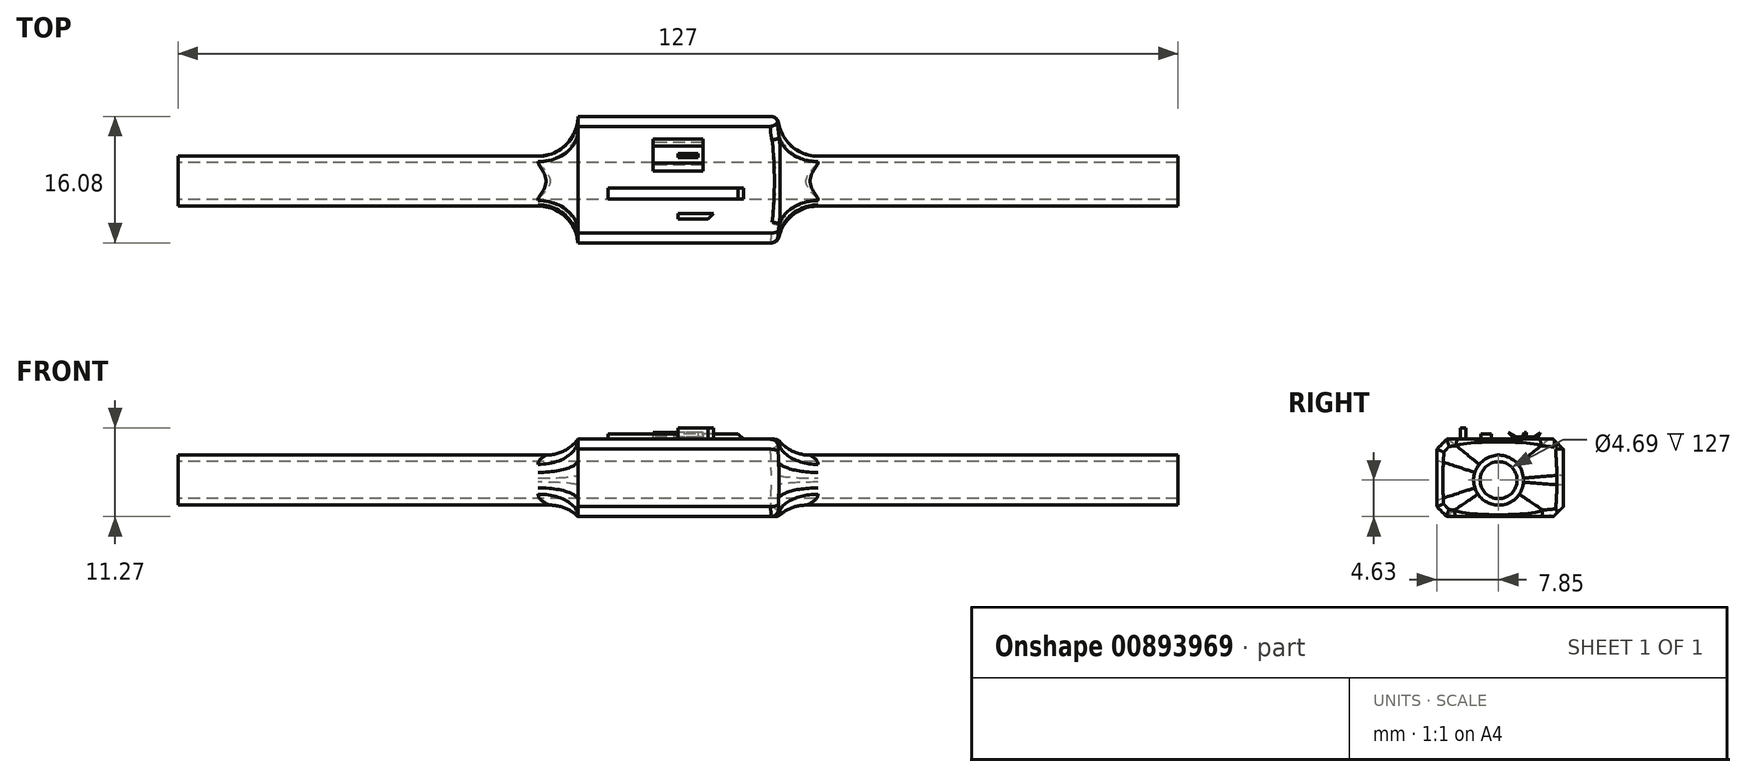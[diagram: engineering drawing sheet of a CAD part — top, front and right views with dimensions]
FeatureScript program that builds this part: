
annotation { "Feature Type Name" : "Feature", "Feature Type Description" : "" }
export const myFeature = defineFeature(function(context is Context, id is Id, definition is map)
    precondition{}
    {
        {
            var Q0;
            Q0=qCreatedBy(makeId("Right.planeOp"),FACE);
            var sketch = newSketch(context, id + "F0", { "sketchPlane" : qUnion([Q0])});
            skCircle(sketch, "E0", {"center": v(0, 0) * mm, "radius": 3.18 * mm});
            skCircle(sketch, "E1", {"center": v(0, 0) * mm, "radius": 2.35 * mm});
            skSolve(sketch);
        }
        {
            var Q0;
            Q0=makeQuery(id+"F0.imprint","IMPRINT",FACE,{"disambiguationData":[TD([[makeQuery(id+"F0.imprint","IMPRINT",EDGE,{"derivedFrom":sQuery(id+"F0.wireOp",EDGE,"E0")}),1.0]])]});
            extrude(context, id + "F1", {"entities" : qUnion([Q0]), "endBound" : BoundingType.SYMMETRIC, "depth" : 127 * mm, "offsetDistance" : 25.4 * mm});
        }
        {
            var Q0;
            Q0=qCreatedBy(makeId("Right.planeOp"),FACE);
            var sketch = newSketch(context, id + "F2", { "sketchPlane" : qUnion([Q0])});
            skLineSegment(sketch, "E2.bottom", {"start": v(-7.85, -4.63) * mm, "end": v(8.23, -4.63) * mm});
            skLineSegment(sketch, "E2.top", {"start": v(-7.85, 5.2) * mm, "end": v(8.23, 5.2) * mm});
            skLineSegment(sketch, "E2.left", {"start": v(-7.85, -4.63) * mm, "end": v(-7.85, 5.2) * mm});
            skLineSegment(sketch, "E2.right", {"start": v(8.23, -4.63) * mm, "end": v(8.23, 5.2) * mm});
            skLineSegment(sketch, "E3", {"start": v(-4.82, 5.2) * mm, "end": v(-4.82, 6.64) * mm});
            skLineSegment(sketch, "E4", {"start": v(-4.82, 6.64) * mm, "end": v(-4.13, 6.64) * mm});
            skLineSegment(sketch, "E5", {"start": v(-4.13, 6.64) * mm, "end": v(-4.13, 5.2) * mm});
            skLineSegment(sketch, "E6", {"start": v(-2.28, 5.2) * mm, "end": v(-2.28, 5.87) * mm});
            skLineSegment(sketch, "E7", {"start": v(-2.28, 5.87) * mm, "end": v(-0.89, 5.87) * mm});
            skLineSegment(sketch, "E8", {"start": v(-0.89, 5.87) * mm, "end": v(-0.89, 5.2) * mm});
            skLineSegment(sketch, "E9", {"start": v(1.27, 6.03) * mm, "end": v(2.06, 5.2) * mm});
            skLineSegment(sketch, "E10", {"start": v(2.06, 5.2) * mm, "end": v(4.9, 5.2) * mm});
            skLineSegment(sketch, "E11", {"start": v(4.9, 5.2) * mm, "end": v(5.31, 6.08) * mm});
            skLineSegment(sketch, "E12", {"start": v(5.31, 6.08) * mm, "end": v(4.47, 5.5) * mm});
            skLineSegment(sketch, "E13", {"start": v(4.47, 5.5) * mm, "end": v(2.3, 5.5) * mm});
            skLineSegment(sketch, "E14", {"start": v(2.3, 5.5) * mm, "end": v(1.27, 6.03) * mm});
            skLineSegment(sketch, "E15", {"start": v(3, 5.5) * mm, "end": v(3.25, 6.03) * mm});
            skLineSegment(sketch, "E16", {"start": v(3.25, 6.03) * mm, "end": v(3.53, 6.03) * mm});
            skLineSegment(sketch, "E17", {"start": v(3.53, 6.03) * mm, "end": v(3.53, 5.5) * mm});
            skCircle(sketch, "E18", {"center": v(0, 0) * mm, "radius": 3.16 * mm});
            skSolve(sketch);
        }
        {
            var Q0;
            Q0=makeQuery(id+"F2.imprint","IMPRINT",FACE,{"disambiguationData":[TD([[makeQuery(id+"F2.imprint","IMPRINT",EDGE,{"derivedFrom":sQuery(id+"F2.wireOp",EDGE,"E2.bottom")}),1.0]])]});
            extrude(context, id + "F3", {"entities" : qUnion([Q0]), "operationType" : NewBodyOperationType.ADD, "endBound" : BoundingType.SYMMETRIC, "depth" : 25.4 * mm, "offsetDistance" : 25.4 * mm});
        }
        {
            var Q0;
            {var subQ0=sQuery(id+"F2.wireOp",EDGE,"E3");Q0=makeQuery(id+"F2.imprint","IMPRINT",FACE,{"disambiguationData":[TD([[makeQuery(id+"F2.imprint","IMPRINT",EDGE,{"derivedFrom":subQ0}),-1.0]])]});}
            extrude(context, id + "F4", {"entities" : qUnion([Q0]), "operationType" : NewBodyOperationType.ADD, "depth" : 5.08 * mm, "offsetDistance" : 25.4 * mm});
        }
        {
            var Q0;
            {var subQ0=sQuery(id+"F2.wireOp",EDGE,"E6");Q0=makeQuery(id+"F2.imprint","IMPRINT",FACE,{"disambiguationData":[TD([[makeQuery(id+"F2.imprint","IMPRINT",EDGE,{"derivedFrom":subQ0}),-1.0]])]});}
            extrude(context, id + "F5", {"entities" : qUnion([Q0]), "operationType" : NewBodyOperationType.ADD, "endBound" : BoundingType.SYMMETRIC, "depth" : 17.78 * mm, "offsetDistance" : 25.4 * mm});
        }
        {
            var Q0;
            Q0=makeQuery(id+"F2.imprint","IMPRINT",FACE,{"disambiguationData":[TD([[makeQuery(id+"F2.imprint","IMPRINT",EDGE,{"derivedFrom":sQuery(id+"F2.wireOp",EDGE,"E9")}),1.0]])]});
            extrude(context, id + "F6", {"entities" : qUnion([Q0]), "operationType" : NewBodyOperationType.ADD, "endBound" : BoundingType.SYMMETRIC, "depth" : 6.35 * mm, "offsetDistance" : 25.4 * mm});
        }
        {
            var Q0;
            {var subQ0=sQuery(id+"F2.wireOp",EDGE,"E15");Q0=makeQuery(id+"F2.imprint","IMPRINT",FACE,{"disambiguationData":[TD([[makeQuery(id+"F2.imprint","IMPRINT",EDGE,{"derivedFrom":subQ0}),-1.0]])]});}
            extrude(context, id + "F7", {"entities" : qUnion([Q0]), "operationType" : NewBodyOperationType.ADD, "depth" : 2.54 * mm, "offsetDistance" : 25.4 * mm});
        }
        {
            var Q0;
            Q0=makeQuery(id+"F3.boolean.opBoolean","INTERSECT",EDGE,{"derivedFrom":[makeQuery(id+"F1.opExtrude","SWEPT_FACE",FACE,{"disambiguationData":[OSD([sQuery(id+"F0.wireOp",EDGE,"E0")])]}),makeQuery(id+"F3.opExtrude","CAP_FACE",FACE,{"disambiguationData":[OSD([sQuery(id+"F2.wireOp",EDGE,"E2.bottom"),sQuery(id+"F2.wireOp",EDGE,"E2.top"),sQuery(id+"F2.wireOp",EDGE,"E2.left"),sQuery(id+"F2.wireOp",EDGE,"E2.right"),sQuery(id+"F2.wireOp",EDGE,"E10")])],"isStart":false})]});
            var Q1;
            Q1=makeQuery(id+"F3.boolean.opBoolean","INTERSECT",EDGE,{"derivedFrom":[makeQuery(id+"F1.opExtrude","SWEPT_FACE",FACE,{"disambiguationData":[OSD([sQuery(id+"F0.wireOp",EDGE,"E0")])]}),makeQuery(id+"F3.opExtrude","CAP_FACE",FACE,{"disambiguationData":[OSD([sQuery(id+"F2.wireOp",EDGE,"E2.bottom"),sQuery(id+"F2.wireOp",EDGE,"E2.top"),sQuery(id+"F2.wireOp",EDGE,"E2.left"),sQuery(id+"F2.wireOp",EDGE,"E2.right"),sQuery(id+"F2.wireOp",EDGE,"E10")])],"isStart":true})]});
            fillet(context, id + "F8", {"entities" : qUnion([Q0, Q1]), "radius" : 5.08 * mm, "tangentPropagation" : true, "allowEdgeOverflow" : false});
        }
        {
            var Q0;
            Q0=makeQuery(id+"F3.opExtrude","SWEPT_EDGE",EDGE,{"disambiguationData":[OSD([sQuery(id+"F2.wireOp",EDGE,"E2.top"),sQuery(id+"F2.wireOp",EDGE,"E2.right")])]});
            var Q1;
            Q1=makeQuery(id+"F3.opExtrude","SWEPT_EDGE",EDGE,{"disambiguationData":[OSD([sQuery(id+"F2.wireOp",EDGE,"E2.bottom"),sQuery(id+"F2.wireOp",EDGE,"E2.right")])]});
            var Q2;
            Q2=makeQuery(id+"F3.opExtrude","SWEPT_EDGE",EDGE,{"disambiguationData":[OSD([sQuery(id+"F2.wireOp",EDGE,"E2.top"),sQuery(id+"F2.wireOp",EDGE,"E2.left")])]});
            var Q3;
            Q3=makeQuery(id+"F3.opExtrude","SWEPT_EDGE",EDGE,{"disambiguationData":[OSD([sQuery(id+"F2.wireOp",EDGE,"E2.bottom"),sQuery(id+"F2.wireOp",EDGE,"E2.left")])]});
            var Q4;
            Q4=makeQuery(id+"F4.opExtrude","CAP_EDGE",EDGE,{"disambiguationData":[OSD([sQuery(id+"F2.wireOp",EDGE,"E3")])],"isStart":false});
            var Q5;
            Q5=makeQuery(id+"F5.opExtrude","CAP_EDGE",EDGE,{"disambiguationData":[OSD([sQuery(id+"F2.wireOp",EDGE,"E7")])],"isStart":false});
            chamfer(context, id + "F9", {"entities" : qUnion([Q0, Q1, Q2, Q3, Q4, Q5]), "width" : 1.27 * mm, "tangentPropagation" : true});
        }
        {
            var Q0;
            {var subQ0=sQuery(id+"F2.wireOp",EDGE,"E10");var subQ1=sQuery(id+"F2.wireOp",EDGE,"E2.top");Q0=makeQuery(id+"F8.opFillet","BLEND_EDGE",EDGE,{"blendedFrom":[makeQuery(id+"F3.boolean.opBoolean","INTERSECT",EDGE,{"derivedFrom":[makeQuery(id+"F1.opExtrude","SWEPT_FACE",FACE,{"disambiguationData":[OSD([sQuery(id+"F0.wireOp",EDGE,"E0")])]}),makeQuery(id+"F3.opExtrude","CAP_FACE",FACE,{"disambiguationData":[OSD([sQuery(id+"F2.wireOp",EDGE,"E2.bottom"),subQ1,sQuery(id+"F2.wireOp",EDGE,"E2.left"),sQuery(id+"F2.wireOp",EDGE,"E2.right"),subQ0,sQuery(id+"F2.wireOp",EDGE,"E18")])],"isStart":false})]}),makeQuery(id+"F3.opExtrude","SWEPT_FACE",FACE,{"disambiguationData":[OSD([subQ1,subQ0])]})],"blendedInto":[makeQuery(id+"F3.opExtrude","SWEPT_FACE",FACE,{"disambiguationData":[OSD([subQ1,subQ0])]})]});}
            var Q1;
            {var subQ0=sQuery(id+"F2.wireOp",EDGE,"E2.left");var subQ1=sQuery(id+"F2.wireOp",EDGE,"E2.top");Q1=makeQuery(id+"F9.opChamfer","BLEND_EDGE",EDGE,{"blendedFrom":[makeQuery(id+"F3.opExtrude","SWEPT_EDGE",EDGE,{"disambiguationData":[OSD([subQ1,subQ0])]}),makeQuery(id+"F8.opFillet","SPLIT",FACE,{"disambiguationData":[OD(2.0)],"derivedFrom":makeQuery(id+"F3.opExtrude","CAP_FACE",FACE,{"disambiguationData":[OSD([sQuery(id+"F2.wireOp",EDGE,"E2.bottom"),subQ1,subQ0,sQuery(id+"F2.wireOp",EDGE,"E2.right"),sQuery(id+"F2.wireOp",EDGE,"E10"),sQuery(id+"F2.wireOp",EDGE,"E18")])],"isStart":false})})],"blendedInto":[makeQuery(id+"F8.opFillet","SPLIT",FACE,{"disambiguationData":[OD(2.0)],"derivedFrom":makeQuery(id+"F3.opExtrude","CAP_FACE",FACE,{"disambiguationData":[OSD([sQuery(id+"F2.wireOp",EDGE,"E2.bottom"),subQ1,subQ0,sQuery(id+"F2.wireOp",EDGE,"E2.right"),sQuery(id+"F2.wireOp",EDGE,"E10"),sQuery(id+"F2.wireOp",EDGE,"E18")])],"isStart":false})})]});}
            var Q2;
            {var subQ0=sQuery(id+"F2.wireOp",EDGE,"E2.left");Q2=makeQuery(id+"F8.opFillet","BLEND_EDGE",EDGE,{"blendedFrom":[makeQuery(id+"F3.boolean.opBoolean","INTERSECT",EDGE,{"derivedFrom":[makeQuery(id+"F1.opExtrude","SWEPT_FACE",FACE,{"disambiguationData":[OSD([sQuery(id+"F0.wireOp",EDGE,"E0")])]}),makeQuery(id+"F3.opExtrude","CAP_FACE",FACE,{"disambiguationData":[OSD([sQuery(id+"F2.wireOp",EDGE,"E2.bottom"),sQuery(id+"F2.wireOp",EDGE,"E2.top"),subQ0,sQuery(id+"F2.wireOp",EDGE,"E2.right"),sQuery(id+"F2.wireOp",EDGE,"E10"),sQuery(id+"F2.wireOp",EDGE,"E18")])],"isStart":false})]}),makeQuery(id+"F3.opExtrude","SWEPT_FACE",FACE,{"disambiguationData":[OSD([subQ0])]})],"blendedInto":[makeQuery(id+"F3.opExtrude","SWEPT_FACE",FACE,{"disambiguationData":[OSD([subQ0])]})]});}
            var Q3;
            Q3=makeQuery(id+"F3.opExtrude","CAP_EDGE",EDGE,{"disambiguationData":[OSD([sQuery(id+"F2.wireOp",EDGE,"E2.left")])],"isStart":false});
            var Q4;
            {var subQ0=sQuery(id+"F2.wireOp",EDGE,"E2.right");var subQ1=sQuery(id+"F2.wireOp",EDGE,"E2.top");Q4=makeQuery(id+"F9.opChamfer","BLEND_EDGE",EDGE,{"blendedFrom":[makeQuery(id+"F3.opExtrude","SWEPT_EDGE",EDGE,{"disambiguationData":[OSD([subQ1,subQ0])]}),makeQuery(id+"F8.opFillet","SPLIT",FACE,{"disambiguationData":[OD(1.0)],"derivedFrom":makeQuery(id+"F3.opExtrude","CAP_FACE",FACE,{"disambiguationData":[OSD([sQuery(id+"F2.wireOp",EDGE,"E2.bottom"),subQ1,sQuery(id+"F2.wireOp",EDGE,"E2.left"),subQ0,sQuery(id+"F2.wireOp",EDGE,"E10"),sQuery(id+"F2.wireOp",EDGE,"E18")])],"isStart":false})})],"blendedInto":[makeQuery(id+"F8.opFillet","SPLIT",FACE,{"disambiguationData":[OD(1.0)],"derivedFrom":makeQuery(id+"F3.opExtrude","CAP_FACE",FACE,{"disambiguationData":[OSD([sQuery(id+"F2.wireOp",EDGE,"E2.bottom"),subQ1,sQuery(id+"F2.wireOp",EDGE,"E2.left"),subQ0,sQuery(id+"F2.wireOp",EDGE,"E10"),sQuery(id+"F2.wireOp",EDGE,"E18")])],"isStart":false})})]});}
            var Q5;
            Q5=makeQuery(id+"F3.opExtrude","CAP_EDGE",EDGE,{"disambiguationData":[OSD([sQuery(id+"F2.wireOp",EDGE,"E2.top"),sQuery(id+"F2.wireOp",EDGE,"E10")])],"isStart":false});
            var Q6;
            {var subQ0=sQuery(id+"F2.wireOp",EDGE,"E2.right");Q6=makeQuery(id+"F8.opFillet","BLEND_EDGE",EDGE,{"blendedFrom":[makeQuery(id+"F3.boolean.opBoolean","INTERSECT",EDGE,{"derivedFrom":[makeQuery(id+"F1.opExtrude","SWEPT_FACE",FACE,{"disambiguationData":[OSD([sQuery(id+"F0.wireOp",EDGE,"E0")])]}),makeQuery(id+"F3.opExtrude","CAP_FACE",FACE,{"disambiguationData":[OSD([sQuery(id+"F2.wireOp",EDGE,"E2.bottom"),sQuery(id+"F2.wireOp",EDGE,"E2.top"),sQuery(id+"F2.wireOp",EDGE,"E2.left"),subQ0,sQuery(id+"F2.wireOp",EDGE,"E10"),sQuery(id+"F2.wireOp",EDGE,"E18")])],"isStart":false})]}),makeQuery(id+"F3.opExtrude","SWEPT_FACE",FACE,{"disambiguationData":[OSD([subQ0])]})],"blendedInto":[makeQuery(id+"F3.opExtrude","SWEPT_FACE",FACE,{"disambiguationData":[OSD([subQ0])]})]});}
            var Q7;
            Q7=makeQuery(id+"F3.opExtrude","CAP_EDGE",EDGE,{"disambiguationData":[OSD([sQuery(id+"F2.wireOp",EDGE,"E2.right")])],"isStart":false});
            var Q8;
            {var subQ0=sQuery(id+"F2.wireOp",EDGE,"E2.right");var subQ1=sQuery(id+"F2.wireOp",EDGE,"E2.bottom");Q8=makeQuery(id+"F9.opChamfer","BLEND_EDGE",EDGE,{"blendedFrom":[makeQuery(id+"F3.opExtrude","SWEPT_EDGE",EDGE,{"disambiguationData":[OSD([subQ1,subQ0])]}),makeQuery(id+"F8.opFillet","SPLIT",FACE,{"disambiguationData":[OD(0.0)],"derivedFrom":makeQuery(id+"F3.opExtrude","CAP_FACE",FACE,{"disambiguationData":[OSD([subQ1,sQuery(id+"F2.wireOp",EDGE,"E2.top"),sQuery(id+"F2.wireOp",EDGE,"E2.left"),subQ0,sQuery(id+"F2.wireOp",EDGE,"E10"),sQuery(id+"F2.wireOp",EDGE,"E18")])],"isStart":false})})],"blendedInto":[makeQuery(id+"F8.opFillet","SPLIT",FACE,{"disambiguationData":[OD(0.0)],"derivedFrom":makeQuery(id+"F3.opExtrude","CAP_FACE",FACE,{"disambiguationData":[OSD([subQ1,sQuery(id+"F2.wireOp",EDGE,"E2.top"),sQuery(id+"F2.wireOp",EDGE,"E2.left"),subQ0,sQuery(id+"F2.wireOp",EDGE,"E10"),sQuery(id+"F2.wireOp",EDGE,"E18")])],"isStart":false})})]});}
            var Q9;
            {var subQ0=sQuery(id+"F2.wireOp",EDGE,"E2.bottom");Q9=makeQuery(id+"F8.opFillet","BLEND_EDGE",EDGE,{"blendedFrom":[makeQuery(id+"F3.boolean.opBoolean","INTERSECT",EDGE,{"derivedFrom":[makeQuery(id+"F1.opExtrude","SWEPT_FACE",FACE,{"disambiguationData":[OSD([sQuery(id+"F0.wireOp",EDGE,"E0")])]}),makeQuery(id+"F3.opExtrude","CAP_FACE",FACE,{"disambiguationData":[OSD([subQ0,sQuery(id+"F2.wireOp",EDGE,"E2.top"),sQuery(id+"F2.wireOp",EDGE,"E2.left"),sQuery(id+"F2.wireOp",EDGE,"E2.right"),sQuery(id+"F2.wireOp",EDGE,"E10"),sQuery(id+"F2.wireOp",EDGE,"E18")])],"isStart":false})]}),makeQuery(id+"F3.opExtrude","SWEPT_FACE",FACE,{"disambiguationData":[OSD([subQ0])]})],"blendedInto":[makeQuery(id+"F3.opExtrude","SWEPT_FACE",FACE,{"disambiguationData":[OSD([subQ0])]})]});}
            var Q10;
            Q10=makeQuery(id+"F3.opExtrude","CAP_EDGE",EDGE,{"disambiguationData":[OSD([sQuery(id+"F2.wireOp",EDGE,"E2.bottom")])],"isStart":false});
            var Q11;
            {var subQ0=sQuery(id+"F2.wireOp",EDGE,"E2.left");var subQ1=sQuery(id+"F2.wireOp",EDGE,"E2.bottom");Q11=makeQuery(id+"F9.opChamfer","BLEND_EDGE",EDGE,{"blendedFrom":[makeQuery(id+"F3.opExtrude","SWEPT_EDGE",EDGE,{"disambiguationData":[OSD([subQ1,subQ0])]}),makeQuery(id+"F8.opFillet","SPLIT",FACE,{"disambiguationData":[OD(3.0)],"derivedFrom":makeQuery(id+"F3.opExtrude","CAP_FACE",FACE,{"disambiguationData":[OSD([subQ1,sQuery(id+"F2.wireOp",EDGE,"E2.top"),subQ0,sQuery(id+"F2.wireOp",EDGE,"E2.right"),sQuery(id+"F2.wireOp",EDGE,"E10"),sQuery(id+"F2.wireOp",EDGE,"E18")])],"isStart":false})})],"blendedInto":[makeQuery(id+"F8.opFillet","SPLIT",FACE,{"disambiguationData":[OD(3.0)],"derivedFrom":makeQuery(id+"F3.opExtrude","CAP_FACE",FACE,{"disambiguationData":[OSD([subQ1,sQuery(id+"F2.wireOp",EDGE,"E2.top"),subQ0,sQuery(id+"F2.wireOp",EDGE,"E2.right"),sQuery(id+"F2.wireOp",EDGE,"E10"),sQuery(id+"F2.wireOp",EDGE,"E18")])],"isStart":false})})]});}
            var Q12;
            {var subQ0=sQuery(id+"F2.wireOp",EDGE,"E18");var subQ1=sQuery(id+"F2.wireOp",EDGE,"E10");var subQ2=sQuery(id+"F2.wireOp",EDGE,"E2.right");var subQ3=sQuery(id+"F2.wireOp",EDGE,"E2.left");var subQ4=sQuery(id+"F2.wireOp",EDGE,"E2.top");var subQ5=sQuery(id+"F2.wireOp",EDGE,"E2.bottom");var subQ6=sQuery(id+"F0.wireOp",EDGE,"E0");Q12=makeQuery(id+"F9.opChamfer","BLEND_EDGE",EDGE,{"blendedFrom":[makeQuery(id+"F3.opExtrude","SWEPT_EDGE",EDGE,{"disambiguationData":[OSD([subQ5,subQ3])]}),makeQuery(id+"F8.opFillet","BLEND_FACE",FACE,{"disambiguationData":[OSD([subQ6,subQ5,subQ4,subQ3,subQ2,subQ1,subQ0]),TDD([makeQuery(id+"F3.boolean.opBoolean","INTERSECT",EDGE,{"derivedFrom":[makeQuery(id+"F1.opExtrude","SWEPT_FACE",FACE,{"disambiguationData":[OSD([subQ6])]}),makeQuery(id+"F3.opExtrude","CAP_FACE",FACE,{"disambiguationData":[OSD([subQ5,subQ4,subQ3,subQ2,subQ1,subQ0])],"isStart":false})]})]),OD(4.0)]})],"blendedInto":[makeQuery(id+"F8.opFillet","BLEND_FACE",FACE,{"disambiguationData":[OSD([subQ6,subQ5,subQ4,subQ3,subQ2,subQ1,subQ0]),TDD([makeQuery(id+"F3.boolean.opBoolean","INTERSECT",EDGE,{"derivedFrom":[makeQuery(id+"F1.opExtrude","SWEPT_FACE",FACE,{"disambiguationData":[OSD([subQ6])]}),makeQuery(id+"F3.opExtrude","CAP_FACE",FACE,{"disambiguationData":[OSD([subQ5,subQ4,subQ3,subQ2,subQ1,subQ0])],"isStart":false})]})]),OD(4.0)]})]});}
            var Q13;
            {var subQ0=sQuery(id+"F2.wireOp",EDGE,"E18");var subQ1=sQuery(id+"F2.wireOp",EDGE,"E10");var subQ2=sQuery(id+"F2.wireOp",EDGE,"E2.right");var subQ3=sQuery(id+"F2.wireOp",EDGE,"E2.left");var subQ4=sQuery(id+"F2.wireOp",EDGE,"E2.top");var subQ5=sQuery(id+"F2.wireOp",EDGE,"E2.bottom");var subQ6=sQuery(id+"F0.wireOp",EDGE,"E0");Q13=makeQuery(id+"F9.opChamfer","BLEND_EDGE",EDGE,{"blendedFrom":[makeQuery(id+"F3.opExtrude","SWEPT_EDGE",EDGE,{"disambiguationData":[OSD([subQ5,subQ3])]}),makeQuery(id+"F8.opFillet","BLEND_FACE",FACE,{"disambiguationData":[OSD([subQ6,subQ5,subQ4,subQ3,subQ2,subQ1,subQ0]),TDD([makeQuery(id+"F3.boolean.opBoolean","INTERSECT",EDGE,{"derivedFrom":[makeQuery(id+"F1.opExtrude","SWEPT_FACE",FACE,{"disambiguationData":[OSD([subQ6])]}),makeQuery(id+"F3.opExtrude","CAP_FACE",FACE,{"disambiguationData":[OSD([subQ5,subQ4,subQ3,subQ2,subQ1,subQ0])],"isStart":false})]})]),OD(0.0)]})],"blendedInto":[makeQuery(id+"F8.opFillet","BLEND_FACE",FACE,{"disambiguationData":[OSD([subQ6,subQ5,subQ4,subQ3,subQ2,subQ1,subQ0]),TDD([makeQuery(id+"F3.boolean.opBoolean","INTERSECT",EDGE,{"derivedFrom":[makeQuery(id+"F1.opExtrude","SWEPT_FACE",FACE,{"disambiguationData":[OSD([subQ6])]}),makeQuery(id+"F3.opExtrude","CAP_FACE",FACE,{"disambiguationData":[OSD([subQ5,subQ4,subQ3,subQ2,subQ1,subQ0])],"isStart":false})]})]),OD(0.0)]})]});}
            fillet(context, id + "F10", {"entities" : qUnion([Q0, Q1, Q2, Q3, Q4, Q5, Q6, Q7, Q8, Q9, Q10, Q11, Q12, Q13]), "radius" : 1 * mm, "tangentPropagation" : true, "allowEdgeOverflow" : false});
        }
    });
